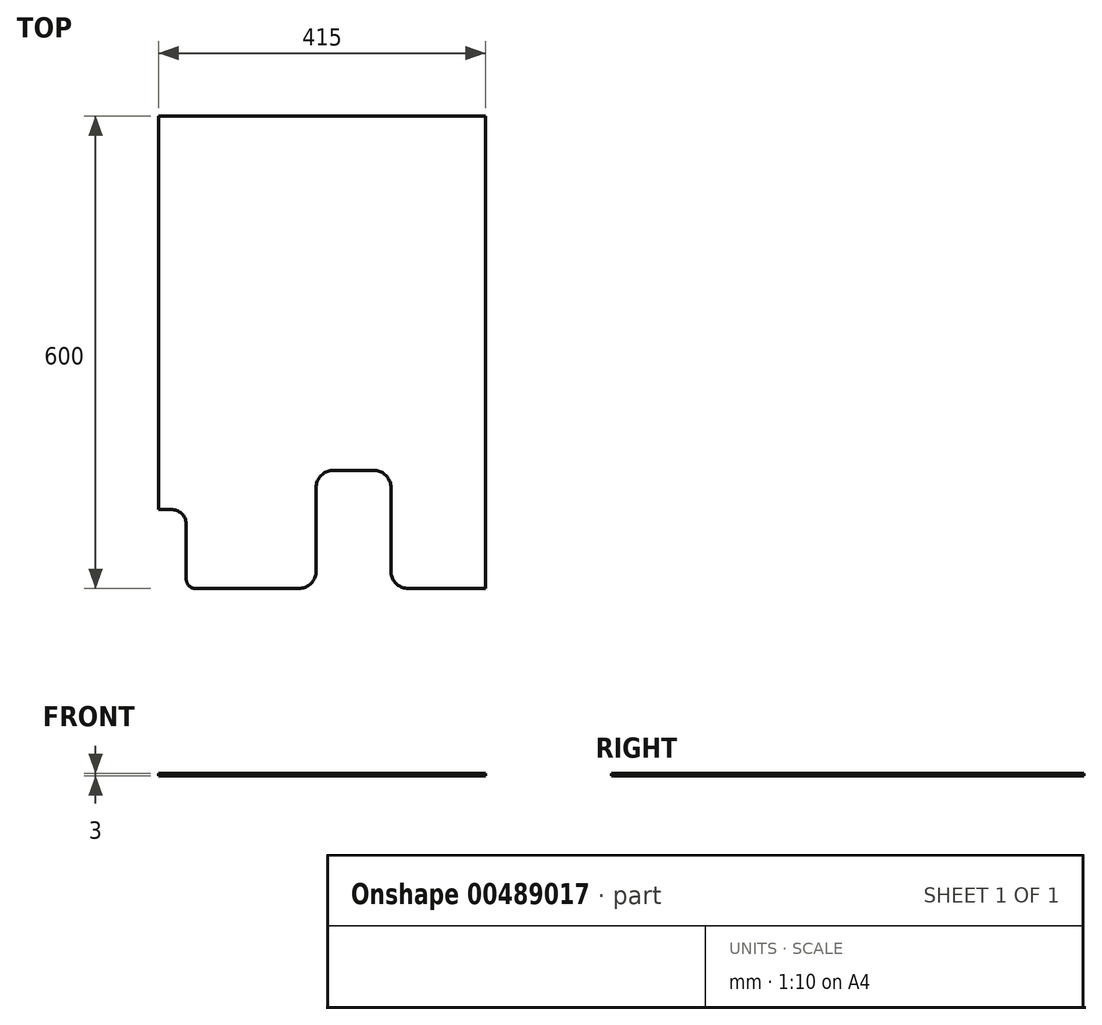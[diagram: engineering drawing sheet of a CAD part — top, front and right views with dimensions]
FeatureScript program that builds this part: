
annotation { "Feature Type Name" : "Feature", "Feature Type Description" : "" }
export const myFeature = defineFeature(function(context is Context, id is Id, definition is map)
    precondition{}
    {
        {
            var Q0;
            Q0=qCreatedBy(makeId("Top.planeOp"),FACE);
            var sketch = newSketch(context, id + "F0", { "sketchPlane" : qUnion([Q0])});
            skLineSegment(sketch, "E0.bottom", {"start": v(-182.13, 405.01) * mm, "end": v(232.87, 405.01) * mm});
            skLineSegment(sketch, "E0.top", {"start": v(-135.62, -194.99) * mm, "end": v(-2.13, -194.99) * mm});
            skLineSegment(sketch, "E0.left", {"start": v(-182.13, 405.01) * mm, "end": v(-182.13, -94.99) * mm});
            skLineSegment(sketch, "E0.right", {"start": v(232.87, 405.01) * mm, "end": v(232.87, -194.99) * mm});
            skLineSegment(sketch, "E1.top", {"start": v(37.87, -44.99) * mm, "end": v(92.87, -44.99) * mm});
            skLineSegment(sketch, "E1.left", {"start": v(17.87, -174.99) * mm, "end": v(17.87, -64.99) * mm});
            skLineSegment(sketch, "E1.right", {"start": v(112.87, -174.99) * mm, "end": v(112.87, -64.99) * mm});
            skArc(sketch, "E2", {"start": v(37.87, -44.99) * mm, "mid": v(24.33, -51.45) * mm, "end": v(17.87, -64.99) * mm});
            skArc(sketch, "E3", {"start": v(112.87, -64.99) * mm, "mid": v(106.4, -51.45) * mm, "end": v(92.87, -44.99) * mm});
            skPoint(sketch, "E4.orphan", {"position": v(17.87, -44.99) * mm});
            skPoint(sketch, "E5.orphan", {"position": v(112.87, -44.99) * mm});
            skArc(sketch, "E6", {"start": v(-2.13, -194.99) * mm, "mid": v(11.4, -188.52) * mm, "end": v(17.87, -174.99) * mm});
            skArc(sketch, "E7", {"start": v(112.87, -174.99) * mm, "mid": v(119.33, -188.52) * mm, "end": v(132.87, -194.99) * mm});
            skLineSegment(sketch, "E8.trimOffspring", {"start": v(132.87, -194.99) * mm, "end": v(232.87, -194.99) * mm});
            skPoint(sketch, "E1.bottom.end.orphan", {"position": v(112.87, -194.99) * mm});
            skPoint(sketch, "E1.bottom.start.orphan", {"position": v(17.87, -194.99) * mm});
            skLineSegment(sketch, "E9", {"start": v(-182.13, -94.99) * mm, "end": v(-164.63, -94.99) * mm});
            skLineSegment(sketch, "E10", {"start": v(-147.13, -112.56) * mm, "end": v(-147.13, -184.47) * mm});
            skArc(sketch, "E11", {"start": v(-147.13, -114.55) * mm, "mid": v(-151.84, -101.15) * mm, "end": v(-164.63, -94.99) * mm});
            skArc(sketch, "E12", {"start": v(-147.13, -181.45) * mm, "mid": v(-144.08, -191.08) * mm, "end": v(-134.77, -194.99) * mm});
            skSolve(sketch);
        }
        {
            var Q0;
            Q0=makeQuery(id+"F0.imprint","IMPRINT",FACE,{"disambiguationData":[TD([[makeQuery(id+"F0.imprint","IMPRINT",EDGE,{"derivedFrom":sQuery(id+"F0.wireOp",EDGE,"E0.bottom")}),-1.0]])]});
            extrude(context, id + "F1", {"entities" : qUnion([Q0]), "depth" : 3 * mm});
        }
    });
